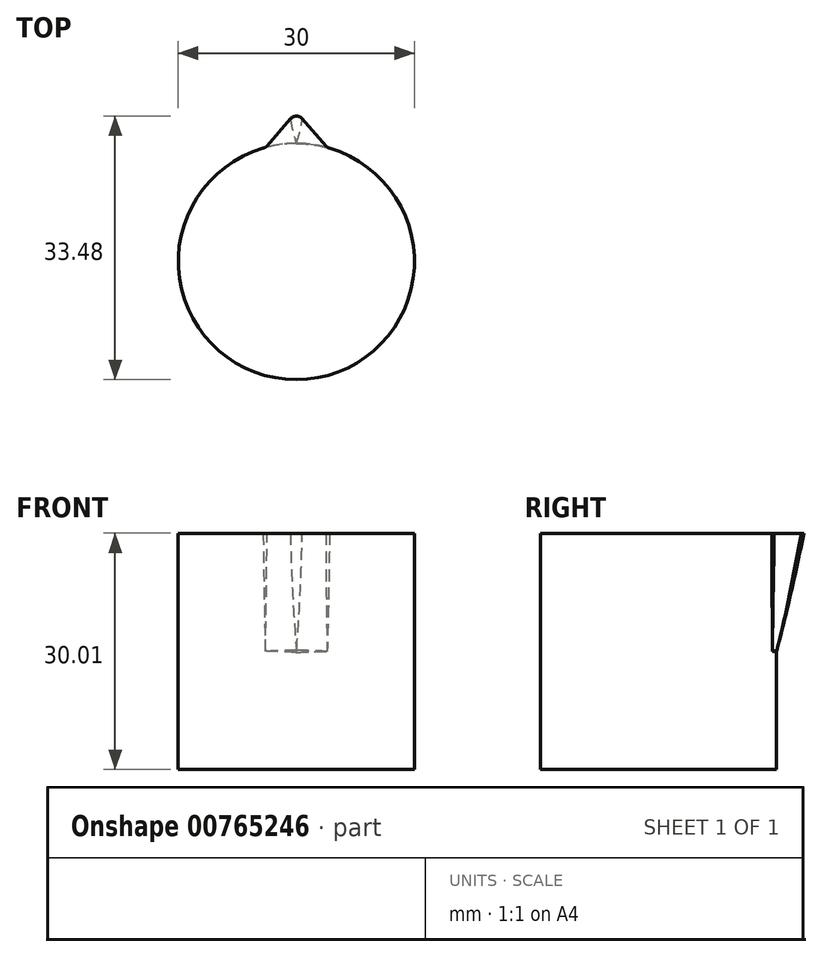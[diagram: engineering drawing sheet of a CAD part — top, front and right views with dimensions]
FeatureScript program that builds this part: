
annotation { "Feature Type Name" : "Feature", "Feature Type Description" : "" }
export const myFeature = defineFeature(function(context is Context, id is Id, definition is map)
    precondition{}
    {
        {
            var Q0;
            Q0=qCreatedBy(makeId("Top.planeOp"),FACE);
            var sketch = newSketch(context, id + "F0", { "sketchPlane" : qUnion([Q0])});
            skCircle(sketch, "E0", {"center": v(-4.16, 0) * mm, "radius": 15 * mm});
            skSolve(sketch);
        }
        {
            var Q0;
            Q0 = qSketchRegion(id + "F0", true);
            extrude(context, id + "F1", {"entities" : qUnion([Q0]), "depth" : 15 * mm, "offsetDistance" : 25 * mm});
        }
        {
            var Q0;
            Q0=makeQuery(id+"F1.opExtrude","CAP_FACE",FACE,{"disambiguationData":[OSD([sQuery(id+"F0.wireOp",EDGE,"E0")])],"isStart":false});
            cPlane(context, id + "F2", {"entities" : qUnion([Q0]), "cplaneType" : CPlaneType.OFFSET, "offset" : 15 * mm, "width" : 150 * mm, "height" : 150 * mm});
        }
        {
            var Q0;
            Q0=qCreatedBy(id+"F2.planeOp",FACE);
            var sketch = newSketch(context, id + "F3", { "sketchPlane" : qUnion([Q0])});
            skArc(sketch, "E1.0", {"start": v(-8.1, 14.47) * mm, "mid": v(-4.16, -15) * mm, "end": v(-0.22, 14.47) * mm});
            skLineSegment(sketch, "E2", {"start": v(-4.16, 19) * mm, "end": v(-8.1, 14.47) * mm});
            skLineSegment(sketch, "E3", {"start": v(-4.16, 19) * mm, "end": v(-0.22, 14.47) * mm});
            skPoint(sketch, "E4.orphan", {"position": v(-4.16, 15) * mm});
            skSolve(sketch);
        }
        {
            var Q0;
            Q0=makeQuery(id+"F1.opExtrude","CAP_FACE",FACE,{"disambiguationData":[OSD([sQuery(id+"F0.wireOp",EDGE,"E0")])],"isStart":false});
            var sketch = newSketch(context, id + "F4", { "sketchPlane" : qUnion([Q0])});
            skArc(sketch, "E5", {"start": v(-8.1, 14.47) * mm, "mid": v(-4.15, -15) * mm, "end": v(-0.24, 14.48) * mm});
            skArc(sketch, "E6", {"start": v(-0.24, 14.48) * mm, "mid": v(-2.18, 14.87) * mm, "end": v(-4.15, 15) * mm});
            skArc(sketch, "E7", {"start": v(-4.15, 15) * mm, "mid": v(-6.15, 14.87) * mm, "end": v(-8.1, 14.47) * mm});
            skSolve(sketch);
        }
        {
            var Q1;
            Q1=makeQuery(id+"F4.imprint","IMPRINT",FACE,{"disambiguationData":[TD([[makeQuery(id+"F4.imprint","IMPRINT",EDGE,{"derivedFrom":sQuery(id+"F4.wireOp",EDGE,"E5")}),1.0]])]});
            var Q2;
            Q2=makeQuery(id+"F3.imprint","IMPRINT",FACE,{"disambiguationData":[TD([[makeQuery(id+"F3.imprint","IMPRINT",EDGE,{"derivedFrom":sQuery(id+"F3.wireOp",EDGE,"E1.0")}),1.0]])]});
            loft(context, id + "F5", {"operationType" : NewBodyOperationType.ADD, "sheetProfilesArray" : [{ "sheetProfileEntities" : qUnion([Q1]) }, { "sheetProfileEntities" : qUnion([Q2]) }]});
        }
        {
            var Q0;
            Q0=makeQuery(id+"F5.opLoft","SWEPT_EDGE",EDGE,{"disambiguationData":[OSD([sQuery(id+"F3.wireOp",EDGE,"E2"),sQuery(id+"F3.wireOp",EDGE,"E3"),sQuery(id+"F4.wireOp",EDGE,"E6"),sQuery(id+"F4.wireOp",EDGE,"E7")])]});
            fillet(context, id + "F6", {"entities" : qUnion([Q0]), "radius" : 1 * mm, "tangentPropagation" : true, "allowEdgeOverflow" : false});
        }
        {
            var Q0;
            Q0=makeQuery(id+"F5.opLoft","SWEPT_EDGE",EDGE,{"disambiguationData":[OSD([sQuery(id+"F3.wireOp",EDGE,"E1.0"),sQuery(id+"F3.wireOp",EDGE,"E2"),sQuery(id+"F4.wireOp",EDGE,"E5"),sQuery(id+"F4.wireOp",EDGE,"E7")])]});
            var Q1;
            Q1=makeQuery(id+"F5.opLoft","SWEPT_EDGE",EDGE,{"disambiguationData":[OSD([sQuery(id+"F3.wireOp",EDGE,"E1.0"),sQuery(id+"F3.wireOp",EDGE,"E3"),sQuery(id+"F4.wireOp",EDGE,"E5"),sQuery(id+"F4.wireOp",EDGE,"E6")])]});
            var Q2;
            {var subQ0=sQuery(id+"F4.wireOp",EDGE,"E7");var subQ1=sQuery(id+"F4.wireOp",EDGE,"E6");var subQ2=sQuery(id+"F4.wireOp",EDGE,"E5");Q2=makeQuery(id+"F5.boolean.opBoolean","MERGE",EDGE,{"derivedFrom":[makeQuery(id+"F1.opExtrude","CAP_EDGE",EDGE,{"disambiguationData":[OSD([sQuery(id+"F0.wireOp",EDGE,"E0")])],"isStart":false}),makeQuery(id+"F5.opLoft","MID_CAP_EDGE",EDGE,{"disambiguationData":[OSD([subQ2,subQ1,subQ0]),TDD([makeQuery(id+"F4.imprint","INTERSECT",VERTEX,{"derivedFrom":[subQ2,subQ0]}),makeQuery(id+"F4.imprint","INTERSECT",VERTEX,{"derivedFrom":[subQ1,subQ0]}),makeQuery(id+"F4.imprint","IMPRINT",EDGE,{"derivedFrom":subQ0})])],"capPos":0.0})]});}
            var Q3;
            {var subQ0=sQuery(id+"F4.wireOp",EDGE,"E6");var subQ1=sQuery(id+"F4.wireOp",EDGE,"E7");var subQ2=sQuery(id+"F4.wireOp",EDGE,"E5");Q3=makeQuery(id+"F5.boolean.opBoolean","MERGE",EDGE,{"derivedFrom":[makeQuery(id+"F1.opExtrude","CAP_EDGE",EDGE,{"disambiguationData":[OSD([sQuery(id+"F0.wireOp",EDGE,"E0")])],"isStart":false}),makeQuery(id+"F5.opLoft","MID_CAP_EDGE",EDGE,{"disambiguationData":[OSD([subQ2,subQ0,subQ1]),TDD([makeQuery(id+"F4.imprint","INTERSECT",VERTEX,{"derivedFrom":[subQ2,subQ0]}),makeQuery(id+"F4.imprint","INTERSECT",VERTEX,{"derivedFrom":[subQ0,subQ1]}),makeQuery(id+"F4.imprint","IMPRINT",EDGE,{"derivedFrom":subQ0})])],"capPos":0.0})]});}
            fillet(context, id + "F7", {"entities" : qUnion([Q0, Q1, Q2, Q3]), "radius" : 1 * mm, "tangentPropagation" : true, "allowEdgeOverflow" : false});
        }
    });
